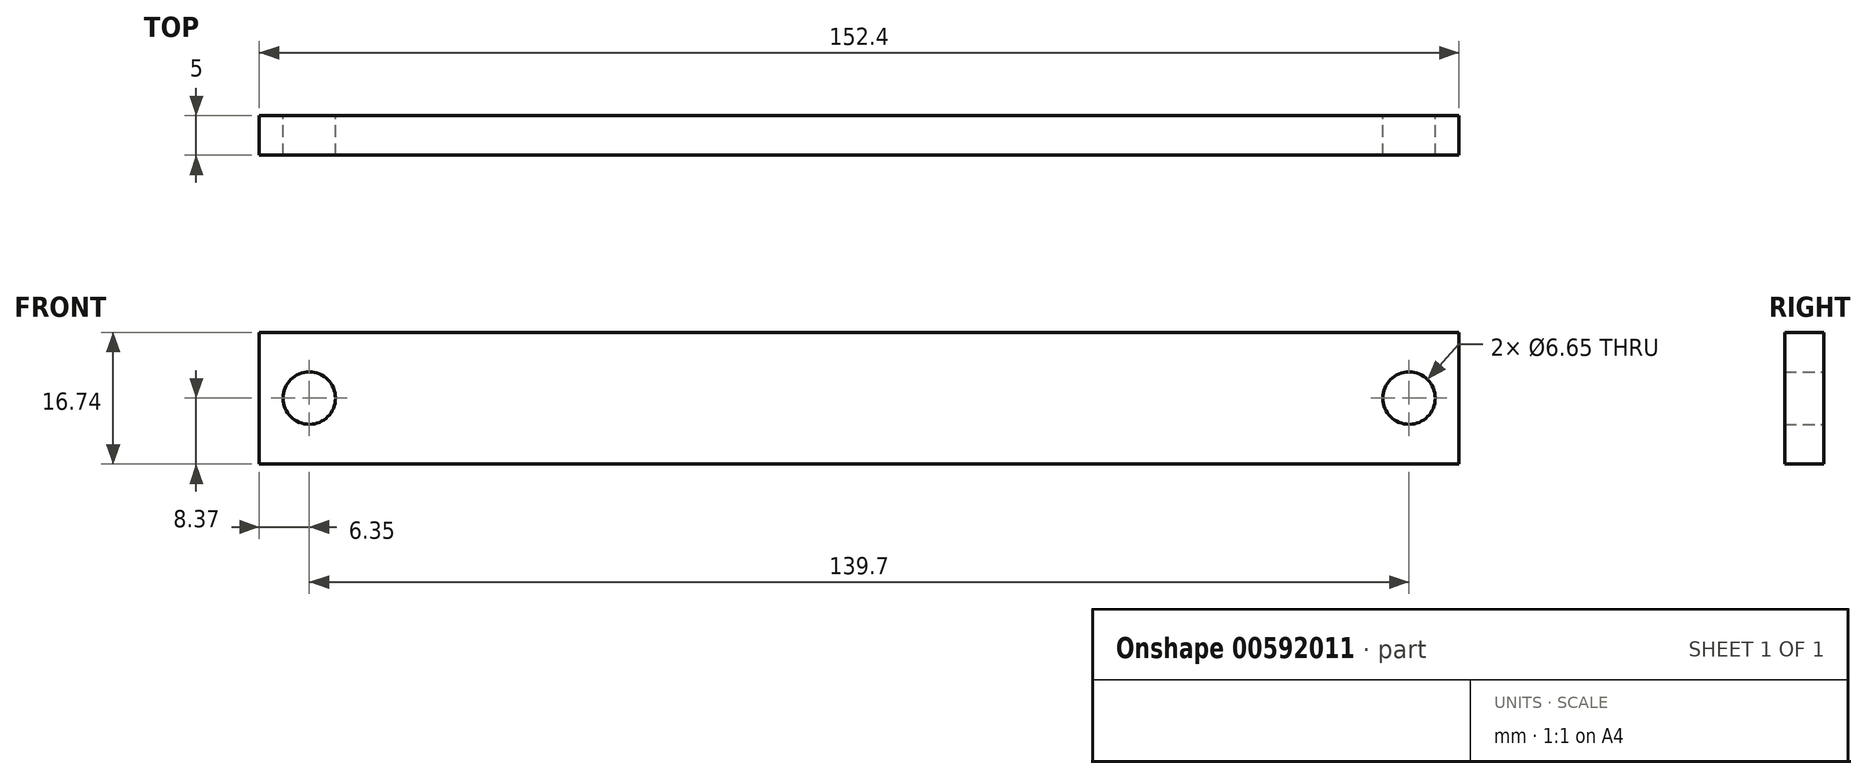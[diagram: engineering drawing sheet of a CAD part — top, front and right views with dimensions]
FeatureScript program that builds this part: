
annotation { "Feature Type Name" : "Feature", "Feature Type Description" : "" }
export const myFeature = defineFeature(function(context is Context, id is Id, definition is map)
    precondition{}
    {
        {
            var Q0;
            Q0=qCreatedBy(makeId("Front.planeOp"),FACE);
            var sketch = newSketch(context, id + "F0", { "sketchPlane" : qUnion([Q0])});
            skLineSegment(sketch, "E0.bottom", {"start": v(76.2, -8.37) * mm, "end": v(-76.2, -8.37) * mm});
            skLineSegment(sketch, "E0.top", {"start": v(76.2, 8.37) * mm, "end": v(-76.2, 8.37) * mm});
            skLineSegment(sketch, "E0.left", {"start": v(76.2, -8.37) * mm, "end": v(76.2, 8.37) * mm});
            skLineSegment(sketch, "E0.right", {"start": v(-76.2, -8.37) * mm, "end": v(-76.2, 8.37) * mm});
            skPoint(sketch, "E0.middle", {"position": v(0, 0) * mm});
            skCircle(sketch, "E1", {"center": v(69.85, 0) * mm, "radius": 3.33 * mm});
            skPoint(sketch, "E1.centerSnap0", {"position": v(76.2, 0) * mm});
            skCircle(sketch, "E2", {"center": v(-69.85, 0) * mm, "radius": 3.33 * mm});
            skSolve(sketch);
        }
        {
            var Q0;
            Q0=makeQuery(id+"F0.imprint","IMPRINT",FACE,{"disambiguationData":[TD([[makeQuery(id+"F0.imprint","IMPRINT",EDGE,{"derivedFrom":sQuery(id+"F0.wireOp",EDGE,"E0.bottom")}),-1.0]])]});
            extrude(context, id + "F1", {"entities" : qUnion([Q0]), "depth" : 5 * mm, "offsetDistance" : 25.4 * mm});
        }
    });
